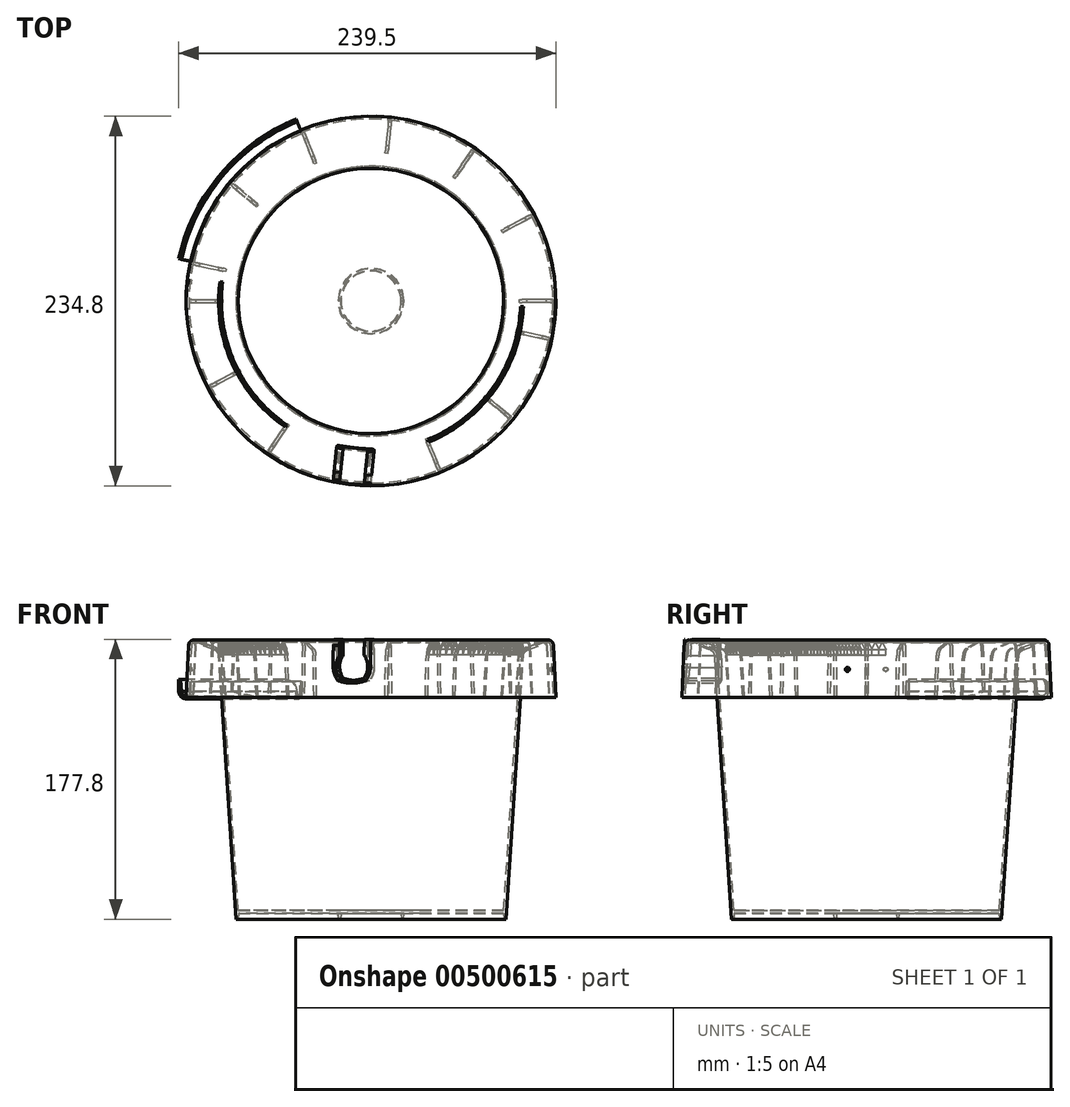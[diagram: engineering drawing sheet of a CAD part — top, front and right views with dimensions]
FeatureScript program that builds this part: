
annotation { "Feature Type Name" : "Feature", "Feature Type Description" : "" }
export const myFeature = defineFeature(function(context is Context, id is Id, definition is map)
    precondition{}
    {
        {
            var Q0;
            Q0=qCreatedBy(makeId("Front.planeOp"),FACE);
            var sketch = newSketch(context, id + "F0", { "sketchPlane" : qUnion([Q0])});
            skLineSegment(sketch, "E0", {"start": v(20.57, 0) * mm, "end": v(19.3, 0) * mm});
            skLineSegment(sketch, "E1", {"start": v(19.3, 0) * mm, "end": v(19.05, 3.81) * mm});
            skLineSegment(sketch, "E2", {"start": v(20.83, 3.81) * mm, "end": v(20.57, 0) * mm});
            skLineSegment(sketch, "E3", {"start": v(0, 0) * mm, "end": v(0, 3.81) * mm});
            skLineSegment(sketch, "E4", {"start": v(0, 3.81) * mm, "end": v(19.05, 3.81) * mm});
            skLineSegment(sketch, "E5", {"start": v(0, 3.81) * mm, "end": v(0, 5.59) * mm});
            skLineSegment(sketch, "E6", {"start": v(0, 5.59) * mm, "end": v(84.3, 5.59) * mm});
            skLineSegment(sketch, "E7", {"start": v(20.83, 3.81) * mm, "end": v(84.3, 3.8) * mm});
            skLineSegment(sketch, "E8", {"start": v(0, 0) * mm, "end": v(0, 179.07) * mm});
            skLineSegment(sketch, "E9", {"start": v(0, 0) * mm, "end": v(0, 171.45) * mm});
            skLineSegment(sketch, "E10", {"start": v(115.62, 140.97) * mm, "end": v(117.4, 140.97) * mm});
            skArc(sketch, "E11", {"start": v(114.08, 174.01) * mm, "mid": v(113.25, 175.47) * mm, "end": v(111.59, 175.66) * mm});
            skLineSegment(sketch, "E12", {"start": v(114.08, 174.01) * mm, "end": v(115.62, 140.97) * mm});
            skLineSegment(sketch, "E13", {"start": v(111.59, 175.66) * mm, "end": v(110.96, 177.33) * mm});
            skLineSegment(sketch, "E14", {"start": v(114.08, 174.01) * mm, "end": v(115.86, 174.1) * mm});
            skLineSegment(sketch, "E15", {"start": v(115.86, 174.1) * mm, "end": v(117.4, 140.97) * mm});
            skArc(sketch, "E16", {"start": v(99.32, 171.08) * mm, "mid": v(97.55, 169.74) * mm, "end": v(96.78, 167.65) * mm});
            skLineSegment(sketch, "E17", {"start": v(96.78, 167.65) * mm, "end": v(85.73, 0) * mm});
            skLineSegment(sketch, "E18", {"start": v(99.32, 171.08) * mm, "end": v(111.59, 175.66) * mm});
            skLineSegment(sketch, "E19", {"start": v(96.78, 167.65) * mm, "end": v(95, 167.77) * mm});
            skLineSegment(sketch, "E20", {"start": v(99.32, 171.08) * mm, "end": v(98.7, 172.74) * mm});
            skLineSegment(sketch, "E21", {"start": v(110.96, 177.33) * mm, "end": v(98.7, 172.74) * mm});
            skLineSegment(sketch, "E22", {"start": v(95, 167.77) * mm, "end": v(84.3, 5.59) * mm});
            skArc(sketch, "E23", {"start": v(98.7, 172.74) * mm, "mid": v(96.12, 170.8) * mm, "end": v(95, 167.77) * mm});
            skLineSegment(sketch, "E24", {"start": v(84.3, 3.8) * mm, "end": v(84.18, 3.8) * mm, "construction": true});
            skLineSegment(sketch, "E25", {"start": v(85.73, 0) * mm, "end": v(84.38, 0) * mm});
            skLineSegment(sketch, "E26", {"start": v(84.18, 3.8) * mm, "end": v(84.38, 0) * mm});
            skLineSegment(sketch, "E27", {"start": v(117.4, 140.97) * mm, "end": v(0, 140.97) * mm, "construction": true});
            skLineSegment(sketch, "E28", {"start": v(95, 167.77) * mm, "end": v(0, 167.77) * mm, "construction": true});
            skLineSegment(sketch, "E29", {"start": v(0, 177.33) * mm, "end": v(0, 179.1) * mm});
            skLineSegment(sketch, "E30", {"start": v(116.18, 167.13) * mm, "end": v(117.96, 167.13) * mm, "construction": true});
            skLineSegment(sketch, "E31", {"start": v(116.18, 167.13) * mm, "end": v(117.96, 167.13) * mm});
            skPoint(sketch, "E32.orphan", {"position": v(120.3, 167.13) * mm});
            skPoint(sketch, "E33.orphan", {"position": v(115.62, 167.13) * mm});
            skLineSegment(sketch, "E34", {"start": v(117.63, 174.1) * mm, "end": v(117.96, 167.13) * mm, "construction": true});
            skLineSegment(sketch, "E35", {"start": v(117.96, 167.13) * mm, "end": v(117.63, 174.1) * mm});
            skPoint(sketch, "E36.start.orphan", {"position": v(115.7, 177.55) * mm});
            skArc(sketch, "E37", {"start": v(117.63, 174.1) * mm, "mid": v(115.95, 177.7) * mm, "end": v(112.23, 179.07) * mm});
            skArc(sketch, "E38", {"start": v(115.86, 174.1) * mm, "mid": v(114.23, 176.96) * mm, "end": v(110.96, 177.33) * mm});
            skSolve(sketch);
        }
        {
            var Q0;
            Q0=qSketchRegion(id+"F0",true);
            var Q1;
            Q1=sQuery(id+"F0.wireOp",EDGE,"E9");
            revolve(context, id + "F1", {"entities" : qUnion([Q0]), "axis" : qUnion([Q1]), "revolveType" : RevolveType.FULL});
        }
        {
            var Q0;
            Q0=qCreatedBy(makeId("Front.planeOp"),FACE);
            var sketch = newSketch(context, id + "F2", { "sketchPlane" : qUnion([Q0])});
            skLineSegment(sketch, "E39", {"start": v(0, 0) * mm, "end": v(0, 3.8) * mm});
            skLineSegment(sketch, "E40", {"start": v(0, 3.8) * mm, "end": v(0, 5.59) * mm});
            skLineSegment(sketch, "E41", {"start": v(0, 0) * mm, "end": v(0, 179.07) * mm});
            skLineSegment(sketch, "E42", {"start": v(0, 0) * mm, "end": v(0, 171.45) * mm});
            skLineSegment(sketch, "E43", {"start": v(0, 179.07) * mm, "end": v(157.98, 179.07) * mm, "construction": true});
            skLineSegment(sketch, "E44", {"start": v(0, 179.07) * mm, "end": v(115.62, 179.07) * mm, "construction": true});
            skLineSegment(sketch, "E45", {"start": v(114.08, 174.01) * mm, "end": v(115.62, 140.97) * mm});
            skLineSegment(sketch, "E46", {"start": v(0, 177.55) * mm, "end": v(129.4, 177.55) * mm, "construction": true});
            skLineSegment(sketch, "E47", {"start": v(111.31, 176.37) * mm, "end": v(99.06, 171.79) * mm});
            skLineSegment(sketch, "E48", {"start": v(94.26, 140.97) * mm, "end": v(96.02, 167.65) * mm});
            skArc(sketch, "E49", {"start": v(99.06, 171.79) * mm, "mid": v(96.93, 170.16) * mm, "end": v(96.02, 167.65) * mm});
            skArc(sketch, "E50", {"start": v(114.08, 174.01) * mm, "mid": v(113.2, 175.8) * mm, "end": v(111.31, 176.37) * mm});
            skLineSegment(sketch, "E51", {"start": v(115.62, 140.97) * mm, "end": v(94.26, 140.97) * mm});
            skSolve(sketch);
        }
        {
            var Q0;
            Q0=makeQuery(id+"F2.imprint","IMPRINT",FACE,{"disambiguationData":[TD([[makeQuery(id+"F2.imprint","IMPRINT",EDGE,{"derivedFrom":sQuery(id+"F2.wireOp",EDGE,"E45")}),-1.0]])]});
            extrude(context, id + "F3", {"entities" : qUnion([Q0]), "endBound" : BoundingType.SYMMETRIC, "depth" : 1.78 * mm});
        }
        {
            var Q0;
            Q0=makeQuery(id+"F3.opExtrude","SWEPT_BODY",BODY,{"disambiguationData":[OSD([sQuery(id+"F2.wireOp",EDGE,"E45"),sQuery(id+"F2.wireOp",EDGE,"E47"),sQuery(id+"F2.wireOp",EDGE,"E48"),sQuery(id+"F2.wireOp",EDGE,"E49"),sQuery(id+"F2.wireOp",EDGE,"E50"),sQuery(id+"F2.wireOp",EDGE,"E51")])]});
            var Q1;
            Q1=makeQuery(id+"F1.opRevolve","SWEPT_FACE",FACE,{"disambiguationData":[OSD([sQuery(id+"F0.wireOp",EDGE,"E15")])]});
            circularPattern(context, id + "F4", {"entities" : qUnion([Q0]), "axis" : qUnion([Q1]), "angle" : 12 * degree, "instanceCount" : 2, "equalSpace" : true});
        }
        {
            var Q0;
            Q0=makeQuery(id+"F3.opExtrude","SWEPT_BODY",BODY,{"disambiguationData":[OSD([sQuery(id+"F2.wireOp",EDGE,"E45"),sQuery(id+"F2.wireOp",EDGE,"E47"),sQuery(id+"F2.wireOp",EDGE,"E48"),sQuery(id+"F2.wireOp",EDGE,"E49"),sQuery(id+"F2.wireOp",EDGE,"E50"),sQuery(id+"F2.wireOp",EDGE,"E51")])]});
            var Q1;
            Q1=makeQuery(id+"F1.opRevolve","SWEPT_FACE",FACE,{"disambiguationData":[OSD([sQuery(id+"F0.wireOp",EDGE,"E12")])]});
            circularPattern(context, id + "F5", {"entities" : qUnion([Q0]), "axis" : qUnion([Q1]), "angle" : 28 * degree, "instanceCount" : 2, "equalSpace" : true});
        }
        {
            var Q0;
            Q0=makeQuery(id+"F3.opExtrude","SWEPT_BODY",BODY,{"disambiguationData":[OSD([sQuery(id+"F2.wireOp",EDGE,"E45"),sQuery(id+"F2.wireOp",EDGE,"E47"),sQuery(id+"F2.wireOp",EDGE,"E48"),sQuery(id+"F2.wireOp",EDGE,"E49"),sQuery(id+"F2.wireOp",EDGE,"E50"),sQuery(id+"F2.wireOp",EDGE,"E51")])]});
            var Q1;
            Q1=makeQuery(id+"F1.opRevolve","SWEPT_FACE",FACE,{"disambiguationData":[OSD([sQuery(id+"F0.wireOp",EDGE,"E12")])]});
            circularPattern(context, id + "F6", {"entities" : qUnion([Q0]), "axis" : qUnion([Q1]), "angle" : 56 * degree, "instanceCount" : 2, "equalSpace" : true});
        }
        {
            var Q0;
            Q0=makeQuery(id+"F3.opExtrude","SWEPT_BODY",BODY,{"disambiguationData":[OSD([sQuery(id+"F2.wireOp",EDGE,"E45"),sQuery(id+"F2.wireOp",EDGE,"E47"),sQuery(id+"F2.wireOp",EDGE,"E48"),sQuery(id+"F2.wireOp",EDGE,"E49"),sQuery(id+"F2.wireOp",EDGE,"E50"),sQuery(id+"F2.wireOp",EDGE,"E51")])]});
            var Q1;
            Q1=makeQuery(id+"F1.opRevolve","SWEPT_FACE",FACE,{"disambiguationData":[OSD([sQuery(id+"F0.wireOp",EDGE,"E12")])]});
            circularPattern(context, id + "F7", {"entities" : qUnion([Q0]), "axis" : qUnion([Q1]), "angle" : 84 * degree, "instanceCount" : 2, "equalSpace" : true});
        }
        {
            var Q0;
            Q0=makeQuery(id+"F1.opRevolve","SWEPT_BODY",BODY,{"disambiguationData":[OSD([sQuery(id+"F0.wireOp",EDGE,"E0"),sQuery(id+"F0.wireOp",EDGE,"E1"),sQuery(id+"F0.wireOp",EDGE,"E2"),sQuery(id+"F0.wireOp",EDGE,"E4"),sQuery(id+"F0.wireOp",EDGE,"E6"),sQuery(id+"F0.wireOp",EDGE,"E7"),sQuery(id+"F0.wireOp",EDGE,"E9"),sQuery(id+"F0.wireOp",EDGE,"E10"),sQuery(id+"F0.wireOp",EDGE,"E11"),sQuery(id+"F0.wireOp",EDGE,"E12"),sQuery(id+"F0.wireOp",EDGE,"E15"),sQuery(id+"F0.wireOp",EDGE,"LKbFe0pn-6IGS-4NvF-Y8YP-ZpA0iSk9hzCY"),sQuery(id+"F0.wireOp",EDGE,"E16"),sQuery(id+"F0.wireOp",EDGE,"E17"),sQuery(id+"F0.wireOp",EDGE,"E18"),sQuery(id+"F0.wireOp",EDGE,"E21"),sQuery(id+"F0.wireOp",EDGE,"E22"),sQuery(id+"F0.wireOp",EDGE,"E23"),sQuery(id+"F0.wireOp",EDGE,"E25"),sQuery(id+"F0.wireOp",EDGE,"E26")])]});
            var Q1;
            Q1=makeQuery(id+"F3.opExtrude","SWEPT_BODY",BODY,{"disambiguationData":[OSD([sQuery(id+"F2.wireOp",EDGE,"E45"),sQuery(id+"F2.wireOp",EDGE,"E47"),sQuery(id+"F2.wireOp",EDGE,"E48"),sQuery(id+"F2.wireOp",EDGE,"E49"),sQuery(id+"F2.wireOp",EDGE,"E50"),sQuery(id+"F2.wireOp",EDGE,"E51")])]});
            var Q2;
            Q2=makeQuery(id+"F1.opRevolve","SWEPT_FACE",FACE,{"disambiguationData":[OSD([sQuery(id+"F0.wireOp",EDGE,"E12")])]});
            circularPattern(context, id + "F8", {"entities" : qUnion([Q0, Q1]), "axis" : qUnion([Q2]), "angle" : 112 * degree, "instanceCount" : 2, "equalSpace" : true});
        }
        {
            var Q0;
            Q0=makeQuery(id+"F3.opExtrude","SWEPT_BODY",BODY,{"disambiguationData":[OSD([sQuery(id+"F2.wireOp",EDGE,"E45"),sQuery(id+"F2.wireOp",EDGE,"E47"),sQuery(id+"F2.wireOp",EDGE,"E48"),sQuery(id+"F2.wireOp",EDGE,"E49"),sQuery(id+"F2.wireOp",EDGE,"E50"),sQuery(id+"F2.wireOp",EDGE,"E51")])]});
            var Q1;
            Q1=makeQuery(id+"F8.opPattern","COPY",FACE,{"derivedFrom":makeQuery(id+"F1.opRevolve","SWEPT_FACE",FACE,{"disambiguationData":[OSD([sQuery(id+"F0.wireOp",EDGE,"E12")])]}),"instanceName":"1"});
            circularPattern(context, id + "F9", {"entities" : qUnion([Q0]), "axis" : qUnion([Q1]), "angle" : 140 * degree, "instanceCount" : 2, "equalSpace" : true});
        }
        {
            var Q0;
            Q0=makeQuery(id+"F3.opExtrude","SWEPT_BODY",BODY,{"disambiguationData":[OSD([sQuery(id+"F2.wireOp",EDGE,"E45"),sQuery(id+"F2.wireOp",EDGE,"E47"),sQuery(id+"F2.wireOp",EDGE,"E48"),sQuery(id+"F2.wireOp",EDGE,"E49"),sQuery(id+"F2.wireOp",EDGE,"E50"),sQuery(id+"F2.wireOp",EDGE,"E51")])]});
            var Q1;
            Q1=makeQuery(id+"F8.opPattern","COPY",FACE,{"derivedFrom":makeQuery(id+"F1.opRevolve","SWEPT_FACE",FACE,{"disambiguationData":[OSD([sQuery(id+"F0.wireOp",EDGE,"E12")])]}),"instanceName":"1"});
            circularPattern(context, id + "F10", {"entities" : qUnion([Q0]), "axis" : qUnion([Q1]), "angle" : 168 * degree, "instanceCount" : 2, "equalSpace" : true});
        }
        {
            var Q0;
            Q0=makeQuery(id+"F3.opExtrude","SWEPT_BODY",BODY,{"disambiguationData":[OSD([sQuery(id+"F2.wireOp",EDGE,"E45"),sQuery(id+"F2.wireOp",EDGE,"E47"),sQuery(id+"F2.wireOp",EDGE,"E48"),sQuery(id+"F2.wireOp",EDGE,"E49"),sQuery(id+"F2.wireOp",EDGE,"E50"),sQuery(id+"F2.wireOp",EDGE,"E51")])]});
            var Q1;
            Q1=makeQuery(id+"F1.opRevolve","SWEPT_FACE",FACE,{"disambiguationData":[OSD([sQuery(id+"F0.wireOp",EDGE,"E11")])]});
            circularPattern(context, id + "F11", {"entities" : qUnion([Q0]), "axis" : qUnion([Q1]), "angle" : 180 * degree, "instanceCount" : 2, "equalSpace" : true});
        }
        {
            var Q0;
            Q0=makeQuery(id+"F3.opExtrude","SWEPT_BODY",BODY,{"disambiguationData":[OSD([sQuery(id+"F2.wireOp",EDGE,"E45"),sQuery(id+"F2.wireOp",EDGE,"E47"),sQuery(id+"F2.wireOp",EDGE,"E48"),sQuery(id+"F2.wireOp",EDGE,"E49"),sQuery(id+"F2.wireOp",EDGE,"E50"),sQuery(id+"F2.wireOp",EDGE,"E51")])]});
            var Q1;
            Q1=makeQuery(id+"F8.opPattern","COPY",FACE,{"derivedFrom":makeQuery(id+"F1.opRevolve","SWEPT_FACE",FACE,{"disambiguationData":[OSD([sQuery(id+"F0.wireOp",EDGE,"E15")])]}),"instanceName":"1"});
            circularPattern(context, id + "F12", {"entities" : qUnion([Q0]), "axis" : qUnion([Q1]), "angle" : 208 * degree, "instanceCount" : 2, "oppositeDirection" : true, "equalSpace" : true});
        }
        {
            var Q0;
            Q0=makeQuery(id+"F3.opExtrude","SWEPT_BODY",BODY,{"disambiguationData":[OSD([sQuery(id+"F2.wireOp",EDGE,"E45"),sQuery(id+"F2.wireOp",EDGE,"E47"),sQuery(id+"F2.wireOp",EDGE,"E48"),sQuery(id+"F2.wireOp",EDGE,"E49"),sQuery(id+"F2.wireOp",EDGE,"E50"),sQuery(id+"F2.wireOp",EDGE,"E51")])]});
            var Q1;
            Q1=makeQuery(id+"F1.opRevolve","SWEPT_FACE",FACE,{"disambiguationData":[OSD([sQuery(id+"F0.wireOp",EDGE,"E15")])]});
            circularPattern(context, id + "F13", {"entities" : qUnion([Q0]), "axis" : qUnion([Q1]), "angle" : 236 * degree, "instanceCount" : 2, "oppositeDirection" : true, "equalSpace" : true});
        }
        {
            var Q0;
            Q0=makeQuery(id+"F3.opExtrude","SWEPT_BODY",BODY,{"disambiguationData":[OSD([sQuery(id+"F2.wireOp",EDGE,"E45"),sQuery(id+"F2.wireOp",EDGE,"E47"),sQuery(id+"F2.wireOp",EDGE,"E48"),sQuery(id+"F2.wireOp",EDGE,"E49"),sQuery(id+"F2.wireOp",EDGE,"E50"),sQuery(id+"F2.wireOp",EDGE,"E51")])]});
            var Q1;
            Q1=makeQuery(id+"F8.opPattern","COPY",FACE,{"derivedFrom":makeQuery(id+"F1.opRevolve","SWEPT_FACE",FACE,{"disambiguationData":[OSD([sQuery(id+"F0.wireOp",EDGE,"E12")])]}),"instanceName":"1"});
            circularPattern(context, id + "F14", {"entities" : qUnion([Q0]), "axis" : qUnion([Q1]), "angle" : 40 * degree, "instanceCount" : 2, "oppositeDirection" : true, "equalSpace" : true});
        }
        {
            var Q0;
            Q0=makeQuery(id+"F3.opExtrude","SWEPT_BODY",BODY,{"disambiguationData":[OSD([sQuery(id+"F2.wireOp",EDGE,"E45"),sQuery(id+"F2.wireOp",EDGE,"E47"),sQuery(id+"F2.wireOp",EDGE,"E48"),sQuery(id+"F2.wireOp",EDGE,"E49"),sQuery(id+"F2.wireOp",EDGE,"E50"),sQuery(id+"F2.wireOp",EDGE,"E51")])]});
            var Q1;
            Q1=makeQuery(id+"F1.opRevolve","SWEPT_FACE",FACE,{"disambiguationData":[OSD([sQuery(id+"F0.wireOp",EDGE,"E12")])]});
            circularPattern(context, id + "F15", {"entities" : qUnion([Q0]), "axis" : qUnion([Q1]), "angle" : 68 * degree, "instanceCount" : 2, "oppositeDirection" : true, "equalSpace" : true});
        }
        {
            var Q0;
            Q0=makeQuery(id+"F4.opPattern","COPY",FACE,{"derivedFrom":makeQuery(id+"F3.opExtrude","CAP_FACE",FACE,{"disambiguationData":[OSD([sQuery(id+"F2.wireOp",EDGE,"E45"),sQuery(id+"F2.wireOp",EDGE,"E47"),sQuery(id+"F2.wireOp",EDGE,"E48"),sQuery(id+"F2.wireOp",EDGE,"E49"),sQuery(id+"F2.wireOp",EDGE,"E50"),sQuery(id+"F2.wireOp",EDGE,"E51")])],"isStart":false}),"instanceName":"1"});
            var Q1;
            Q1=makeQuery(id+"F3.opExtrude","CAP_FACE",FACE,{"disambiguationData":[OSD([sQuery(id+"F2.wireOp",EDGE,"E45"),sQuery(id+"F2.wireOp",EDGE,"E47"),sQuery(id+"F2.wireOp",EDGE,"E48"),sQuery(id+"F2.wireOp",EDGE,"E49"),sQuery(id+"F2.wireOp",EDGE,"E50"),sQuery(id+"F2.wireOp",EDGE,"E51")])],"isStart":true});
            cPlane(context, id + "F16", {"entities" : qUnion([Q0, Q1]), "cplaneType" : CPlaneType.MID_PLANE, "offset" : 25.4 * mm, "width" : 152.4 * mm, "height" : 152.4 * mm});
        }
        {
            var Q0;
            Q0=qCreatedBy(id+"F16.planeOp",FACE);
            cPlane(context, id + "F17", {"entities" : qUnion([Q0]), "cplaneType" : CPlaneType.OFFSET, "offset" : 127 * mm, "width" : 152.4 * mm, "height" : 152.4 * mm});
        }
        {
            var Q0;
            Q0=makeQuery(id+"F7.opPattern","COPY",FACE,{"derivedFrom":makeQuery(id+"F3.opExtrude","CAP_FACE",FACE,{"disambiguationData":[OSD([sQuery(id+"F2.wireOp",EDGE,"E45"),sQuery(id+"F2.wireOp",EDGE,"E47"),sQuery(id+"F2.wireOp",EDGE,"E48"),sQuery(id+"F2.wireOp",EDGE,"E49"),sQuery(id+"F2.wireOp",EDGE,"E50"),sQuery(id+"F2.wireOp",EDGE,"E51")])],"isStart":false}),"instanceName":"1"});
            cPlane(context, id + "F18", {"entities" : qUnion([Q0]), "cplaneType" : CPlaneType.OFFSET, "offset" : 0.89 * mm, "oppositeDirection" : true, "width" : 152.4 * mm, "height" : 152.4 * mm});
        }
        {
            var Q0;
            Q0=qCreatedBy(id+"F18.planeOp",FACE);
            cPlane(context, id + "F19", {"entities" : qUnion([Q0]), "cplaneType" : CPlaneType.OFFSET, "offset" : 127 * mm, "width" : 152.4 * mm, "height" : 152.4 * mm});
        }
        {
            var Q0;
            Q0=qCreatedBy(id+"F19.planeOp",FACE);
            var sketch = newSketch(context, id + "F20", { "sketchPlane" : qUnion([Q0])});
            skLineSegment(sketch, "E52", {"start": v(0, 0) * mm, "end": v(0, 158.75) * mm, "construction": true});
            skCircle(sketch, "E53", {"center": v(0, 158.75) * mm, "radius": 1.27 * mm});
            skSolve(sketch);
        }
        {
            var Q0;
            Q0=makeQuery(id+"F20.imprint","IMPRINT",FACE,{"disambiguationData":[TD([[makeQuery(id+"F20.imprint","IMPRINT",EDGE,{"derivedFrom":sQuery(id+"F20.wireOp",EDGE,"E53")}),1.0]])]});
            extrude(context, id + "F21", {"entities" : qUnion([Q0]), "operationType" : NewBodyOperationType.REMOVE, "oppositeDirection" : true, "depth" : 25.4 * mm});
        }
        {
            var Q0;
            Q0=qCreatedBy(id+"F19.planeOp",FACE);
            cPlane(context, id + "F22", {"entities" : qUnion([Q0]), "cplaneType" : CPlaneType.OFFSET, "offset" : 254 * mm, "oppositeDirection" : true, "width" : 152.4 * mm, "height" : 152.4 * mm});
        }
        {
            var Q0;
            Q0=qCreatedBy(id+"F22.planeOp",FACE);
            var sketch = newSketch(context, id + "F23", { "sketchPlane" : qUnion([Q0])});
            skLineSegment(sketch, "E54", {"start": v(0, 0) * mm, "end": v(0, 158.75) * mm, "construction": true});
            skCircle(sketch, "E55", {"center": v(0, 158.75) * mm, "radius": 1.27 * mm});
            skSolve(sketch);
        }
        {
            var Q0;
            Q0=makeQuery(id+"F23.imprint","IMPRINT",FACE,{"disambiguationData":[TD([[makeQuery(id+"F23.imprint","IMPRINT",EDGE,{"derivedFrom":sQuery(id+"F23.wireOp",EDGE,"E55")}),1.0]])]});
            extrude(context, id + "F24", {"entities" : qUnion([Q0]), "operationType" : NewBodyOperationType.REMOVE, "depth" : 25.4 * mm});
        }
        {
            var Q0;
            Q0=qCreatedBy(id+"F17.planeOp",FACE);
            cPlane(context, id + "F25", {"entities" : qUnion([Q0]), "cplaneType" : CPlaneType.OFFSET, "offset" : 25.4 * mm, "oppositeDirection" : true, "width" : 152.4 * mm, "height" : 152.4 * mm});
        }
        {
            var Q0;
            Q0=qCreatedBy(id+"F16.planeOp",FACE);
            var sketch = newSketch(context, id + "F26", { "sketchPlane" : qUnion([Q0])});
            skLineSegment(sketch, "E56", {"start": v(0, 0) * mm, "end": v(-95, 0) * mm, "construction": true});
            skLineSegment(sketch, "E57", {"start": v(-95, 0) * mm, "end": v(-95, 167.77) * mm, "construction": true});
            skLineSegment(sketch, "E58", {"start": v(-95, 167.77) * mm, "end": v(-95, 176.02) * mm});
            skLineSegment(sketch, "E59", {"start": v(-95, 176.02) * mm, "end": v(-96.77, 176.02) * mm});
            skLineSegment(sketch, "E60", {"start": v(-96.77, 176.02) * mm, "end": v(-96.77, 171.3) * mm});
            skLineSegment(sketch, "E61", {"start": v(-95, 167.77) * mm, "end": v(-96.77, 171.3) * mm});
            skSolve(sketch);
        }
        {
            var Q0;
            Q0=makeQuery(id+"F26.imprint","IMPRINT",FACE,{"disambiguationData":[TD([[makeQuery(id+"F26.imprint","IMPRINT",EDGE,{"derivedFrom":sQuery(id+"F26.wireOp",EDGE,"E58")}),1.0]])]});
            extrude(context, id + "F27", {"entities" : qUnion([Q0]), "depth" : 2.22 * mm, "hasSecondDirection" : true, "secondDirectionOppositeDirection" : true, "secondDirectionDepth" : 2.22 * mm});
        }
        {
            var Q0;
            Q0=makeQuery(id+"F27.opExtrude","SWEPT_FACE",FACE,{"disambiguationData":[OSD([sQuery(id+"F26.wireOp",EDGE,"E60")])]});
            var sketch = newSketch(context, id + "F28", { "sketchPlane" : qUnion([Q0])});
            skLineSegment(sketch, "E62", {"start": v(2.22, 176.02) * mm, "end": v(2.22, 171.63) * mm});
            skLineSegment(sketch, "E63", {"start": v(2.22, 171.63) * mm, "end": v(0, 176.02) * mm});
            skLineSegment(sketch, "E64", {"start": v(0, 176.02) * mm, "end": v(2.22, 176.02) * mm});
            skSolve(sketch);
        }
        {
            var Q0;
            Q0=makeQuery(id+"F28.imprint","IMPRINT",FACE,{"disambiguationData":[TD([[makeQuery(id+"F28.imprint","IMPRINT",EDGE,{"derivedFrom":sQuery(id+"F28.wireOp",EDGE,"E62")}),-1.0]])]});
            extrude(context, id + "F29", {"entities" : qUnion([Q0]), "operationType" : NewBodyOperationType.REMOVE, "oppositeDirection" : true, "depth" : 25.4 * mm});
        }
        {
            var Q0;
            Q0=makeQuery(id+"F27.opExtrude","SWEPT_FACE",FACE,{"disambiguationData":[OSD([sQuery(id+"F26.wireOp",EDGE,"E60")])]});
            var sketch = newSketch(context, id + "F30", { "sketchPlane" : qUnion([Q0])});
            skLineSegment(sketch, "E65", {"start": v(0, 176.02) * mm, "end": v(-2.22, 176.02) * mm});
            skLineSegment(sketch, "E66", {"start": v(-2.22, 176.02) * mm, "end": v(-2.22, 171.64) * mm});
            skLineSegment(sketch, "E67", {"start": v(-2.22, 171.64) * mm, "end": v(0, 176.02) * mm});
            skSolve(sketch);
        }
        {
            var Q0;
            Q0=makeQuery(id+"F30.imprint","IMPRINT",FACE,{"disambiguationData":[TD([[makeQuery(id+"F30.imprint","IMPRINT",EDGE,{"derivedFrom":sQuery(id+"F30.wireOp",EDGE,"E65")}),1.0]])]});
            extrude(context, id + "F31", {"entities" : qUnion([Q0]), "operationType" : NewBodyOperationType.REMOVE, "oppositeDirection" : true, "depth" : 25.4 * mm});
        }
        {
            var Q0;
            Q0=makeQuery(id+"F27.opExtrude","SWEPT_BODY",BODY,{"disambiguationData":[OSD([sQuery(id+"F26.wireOp",EDGE,"E58"),sQuery(id+"F26.wireOp",EDGE,"E59"),sQuery(id+"F26.wireOp",EDGE,"E60"),sQuery(id+"F26.wireOp",EDGE,"E61")])]});
            var Q1;
            Q1=makeQuery(id+"F1.opRevolve","SWEPT_FACE",FACE,{"disambiguationData":[OSD([sQuery(id+"F0.wireOp",EDGE,"E22")])]});
            circularPattern(context, id + "F32", {"entities" : qUnion([Q0]), "axis" : qUnion([Q1]), "angle" : 60.5 * degree, "instanceCount" : 24, "oppositeDirection" : true, "equalSpace" : true});
        }
        {
            var Q0;
            Q0=makeQuery(id+"F32.opPattern","COPY",BODY,{"derivedFrom":makeQuery(id+"F27.opExtrude","SWEPT_BODY",BODY,{"disambiguationData":[OSD([sQuery(id+"F26.wireOp",EDGE,"E58"),sQuery(id+"F26.wireOp",EDGE,"E59"),sQuery(id+"F26.wireOp",EDGE,"E60"),sQuery(id+"F26.wireOp",EDGE,"E61")])]}),"instanceName":"1"});
            var Q1;
            Q1=makeQuery(id+"F27.opExtrude","SWEPT_BODY",BODY,{"disambiguationData":[OSD([sQuery(id+"F26.wireOp",EDGE,"E58"),sQuery(id+"F26.wireOp",EDGE,"E59"),sQuery(id+"F26.wireOp",EDGE,"E60"),sQuery(id+"F26.wireOp",EDGE,"E61")])]});
            var Q2;
            Q2=makeQuery(id+"F8.opPattern","COPY",FACE,{"derivedFrom":makeQuery(id+"F1.opRevolve","SWEPT_FACE",FACE,{"disambiguationData":[OSD([sQuery(id+"F0.wireOp",EDGE,"E15")])]}),"instanceName":"1"});
            circularPattern(context, id + "F33", {"entities" : qUnion([Q0, Q1]), "axis" : qUnion([Q2]), "angle" : 180 * degree, "instanceCount" : 2, "oppositeDirection" : true, "equalSpace" : true});
        }
        {
            var Q0;
            Q0=makeQuery(id+"F33.opPattern","COPY",BODY,{"derivedFrom":makeQuery(id+"F32.opPattern","COPY",BODY,{"derivedFrom":makeQuery(id+"F27.opExtrude","SWEPT_BODY",BODY,{"disambiguationData":[OSD([sQuery(id+"F26.wireOp",EDGE,"E58"),sQuery(id+"F26.wireOp",EDGE,"E59"),sQuery(id+"F26.wireOp",EDGE,"E60"),sQuery(id+"F26.wireOp",EDGE,"E61")])]}),"instanceName":"1"}),"instanceName":"1"});
            var Q1;
            Q1=makeQuery(id+"F33.opPattern","COPY",BODY,{"derivedFrom":makeQuery(id+"F27.opExtrude","SWEPT_BODY",BODY,{"disambiguationData":[OSD([sQuery(id+"F26.wireOp",EDGE,"E58"),sQuery(id+"F26.wireOp",EDGE,"E59"),sQuery(id+"F26.wireOp",EDGE,"E60"),sQuery(id+"F26.wireOp",EDGE,"E61")])]}),"instanceName":"1"});
            var Q2;
            Q2=makeQuery(id+"F1.opRevolve","SWEPT_FACE",FACE,{"disambiguationData":[OSD([sQuery(id+"F0.wireOp",EDGE,"E21")])]});
            circularPattern(context, id + "F34", {"entities" : qUnion([Q0, Q1]), "axis" : qUnion([Q2]), "angle" : 60.5 * degree, "instanceCount" : 24, "equalSpace" : true});
        }
        {
            var Q0;
            Q0=makeQuery(id+"F10.opPattern","COPY",FACE,{"derivedFrom":makeQuery(id+"F3.opExtrude","CAP_FACE",FACE,{"disambiguationData":[OSD([sQuery(id+"F2.wireOp",EDGE,"E45"),sQuery(id+"F2.wireOp",EDGE,"E47"),sQuery(id+"F2.wireOp",EDGE,"E48"),sQuery(id+"F2.wireOp",EDGE,"E49"),sQuery(id+"F2.wireOp",EDGE,"E50"),sQuery(id+"F2.wireOp",EDGE,"E51")])],"isStart":false}),"instanceName":"1"});
            var sketch = newSketch(context, id + "F35", { "sketchPlane" : qUnion([Q0])});
            skLineSegment(sketch, "E68", {"start": v(115.5, 140.97) * mm, "end": v(115.05, 151.12) * mm});
            skLineSegment(sketch, "E69", {"start": v(117.3, 151.12) * mm, "end": v(118.28, 141.1) * mm});
            skLineSegment(sketch, "E70", {"start": v(117.3, 151.12) * mm, "end": v(115.05, 151.12) * mm});
            skLineSegment(sketch, "E71", {"start": v(118.28, 141.1) * mm, "end": v(118.46, 139.23) * mm});
            skLineSegment(sketch, "E72", {"start": v(115.5, 140.97) * mm, "end": v(115.5, 139.25) * mm});
            skLineSegment(sketch, "E73", {"start": v(115.5, 139.25) * mm, "end": v(118.46, 139.23) * mm});
            skSolve(sketch);
        }
        {
            var Q0;
            {var subQ2=sQuery(id+"F35.wireOp",EDGE,"E69");Q0=makeQuery(id+"F35.imprint","IMPRINT",FACE,{"disambiguationData":[TD([[makeQuery(id+"F35.imprint","IMPRINT",EDGE,{"derivedFrom":subQ2}),-1.0]])]});}
            var Q1;
            Q1=makeQuery(id+"F8.opPattern","COPY",FACE,{"derivedFrom":makeQuery(id+"F1.opRevolve","SWEPT_FACE",FACE,{"disambiguationData":[OSD([sQuery(id+"F0.wireOp",EDGE,"E15")])]}),"instanceName":"1"});
            revolve(context, id + "F36", {"operationType" : NewBodyOperationType.REMOVE, "entities" : qUnion([Q0]), "axis" : qUnion([Q1]), "revolveType" : RevolveType.ONE_DIRECTION, "angle" : 55 * degree});
        }
        {
            var Q0;
            {var subQ0=sQuery(id+"F35.wireOp",EDGE,"E70");Q0=makeQuery(id+"F36.boolean.opBoolean","COPY",FACE,{"disambiguationData":[TD([makeQuery(id+"F8.opPattern","COPY",FACE,{"derivedFrom":makeQuery(id+"F1.opRevolve","SWEPT_FACE",FACE,{"disambiguationData":[OSD([sQuery(id+"F0.wireOp",EDGE,"E10")])]}),"instanceName":"1"})])],"derivedFrom":makeQuery(id+"F36.opRevolve","CAP_FACE",FACE,{"disambiguationData":[OSD([sQuery(id+"F2.wireOp",EDGE,"E45"),sQuery(id+"F2.wireOp",EDGE,"E51"),sQuery(id+"F35.wireOp",EDGE,"E69"),subQ0,sQuery(id+"F35.wireOp",EDGE,"E71"),sQuery(id+"F35.wireOp",EDGE,"E72"),sQuery(id+"F35.wireOp",EDGE,"E73")])],"isStart":true})});}
            var sketch = newSketch(context, id + "F37", { "sketchPlane" : qUnion([Q0])});
            skLineSegment(sketch, "E74", {"start": v(115.62, 140.97) * mm, "end": v(125.02, 140.97) * mm, "construction": true});
            skLineSegment(sketch, "E75", {"start": v(115.62, 140.97) * mm, "end": v(120.32, 140.97) * mm, "construction": true});
            skLineSegment(sketch, "E76", {"start": v(116.92, 151.12) * mm, "end": v(115.15, 151.12) * mm});
            skLineSegment(sketch, "E77", {"start": v(115.15, 151.12) * mm, "end": v(115.44, 144.83) * mm});
            skLineSegment(sketch, "E78", {"start": v(115.44, 144.83) * mm, "end": v(115.44, 144.83) * mm});
            skArc(sketch, "E79", {"start": v(115.44, 144.83) * mm, "mid": v(120.23, 140.04) * mm, "end": v(125.02, 144.83) * mm});
            skLineSegment(sketch, "E80", {"start": v(125.02, 152.45) * mm, "end": v(123.75, 152.45) * mm});
            skLineSegment(sketch, "E81", {"start": v(123.75, 152.45) * mm, "end": v(123.24, 144.83) * mm});
            skLineSegment(sketch, "E82", {"start": v(120.23, 140.97) * mm, "end": v(120.23, 141.82) * mm});
            skArc(sketch, "E83", {"start": v(117.22, 144.83) * mm, "mid": v(120.23, 141.82) * mm, "end": v(123.24, 144.83) * mm});
            skLineSegment(sketch, "E84", {"start": v(116.92, 151.12) * mm, "end": v(117.22, 144.83) * mm});
            skPoint(sketch, "E85.orphan", {"position": v(120.23, 140.04) * mm});
            skLineSegment(sketch, "E86", {"start": v(125.02, 152.45) * mm, "end": v(125.02, 144.83) * mm});
            skSolve(sketch);
        }
        {
            var Q0;
            Q0=makeQuery(id+"F37.imprint","IMPRINT",FACE,{"disambiguationData":[TD([[makeQuery(id+"F37.imprint","IMPRINT",EDGE,{"derivedFrom":sQuery(id+"F37.wireOp",EDGE,"E80")}),1.0]])]});
            var Q1;
            Q1=makeQuery(id+"F37.imprint","IMPRINT",FACE,{"disambiguationData":[TD([[makeQuery(id+"F37.imprint","IMPRINT",EDGE,{"derivedFrom":sQuery(id+"F37.wireOp",EDGE,"E76")}),1.0]])]});
            var Q2;
            Q2=makeQuery(id+"F1.opRevolve","SWEPT_FACE",FACE,{"disambiguationData":[OSD([sQuery(id+"F0.wireOp",EDGE,"E15")])]});
            revolve(context, id + "F38", {"entities" : qUnion([Q0, Q1]), "axis" : qUnion([Q2]), "revolveType" : RevolveType.ONE_DIRECTION, "angle" : 55.2 * degree});
        }
        {
            var Q0;
            Q0=makeQuery(id+"F38.opRevolve","CAP_EDGE",EDGE,{"disambiguationData":[OSD([sQuery(id+"F37.wireOp",EDGE,"E80")]),OD(0.0)],"isStart":false});
            var Q1;
            Q1=makeQuery(id+"F38.opRevolve","CAP_EDGE",EDGE,{"disambiguationData":[OSD([sQuery(id+"F37.wireOp",EDGE,"E80")]),OD(1.0)],"isStart":false});
            fillet(context, id + "F39", {"entities" : qUnion([Q0, Q1]), "radius" : 7.62 * mm, "tangentPropagation" : true, "allowEdgeOverflow" : false});
        }
        {
            var Q0;
            Q0=makeQuery(id+"F9.opPattern","COPY",FACE,{"derivedFrom":makeQuery(id+"F3.opExtrude","CAP_FACE",FACE,{"disambiguationData":[OSD([sQuery(id+"F2.wireOp",EDGE,"E45"),sQuery(id+"F2.wireOp",EDGE,"E47"),sQuery(id+"F2.wireOp",EDGE,"E48"),sQuery(id+"F2.wireOp",EDGE,"E49"),sQuery(id+"F2.wireOp",EDGE,"E50"),sQuery(id+"F2.wireOp",EDGE,"E51")])],"isStart":true}),"instanceName":"1"});
            var sketch = newSketch(context, id + "F40", { "sketchPlane" : qUnion([Q0])});
            skLineSegment(sketch, "E87", {"start": v(-115.36, 144.6) * mm, "end": v(-115.62, 140.97) * mm});
            skLineSegment(sketch, "E88", {"start": v(-115.62, 140.97) * mm, "end": v(-94.98, 140.97) * mm});
            skLineSegment(sketch, "E89", {"start": v(-94.98, 140.97) * mm, "end": v(-115.36, 144.6) * mm});
            skSolve(sketch);
        }
        {
            var Q0;
            Q0=makeQuery(id+"F40.imprint","IMPRINT",FACE,{"disambiguationData":[TD([[makeQuery(id+"F40.imprint","IMPRINT",EDGE,{"derivedFrom":sQuery(id+"F40.wireOp",EDGE,"E87")}),1.0]])]});
            extrude(context, id + "F41", {"entities" : qUnion([Q0]), "operationType" : NewBodyOperationType.REMOVE, "oppositeDirection" : true, "depth" : 1.78 * mm});
        }
        {
            var Q0;
            Q0=makeQuery(id+"F9.opPattern","COPY",FACE,{"derivedFrom":makeQuery(id+"F3.opExtrude","CAP_FACE",FACE,{"disambiguationData":[OSD([sQuery(id+"F2.wireOp",EDGE,"E45"),sQuery(id+"F2.wireOp",EDGE,"E47"),sQuery(id+"F2.wireOp",EDGE,"E48"),sQuery(id+"F2.wireOp",EDGE,"E49"),sQuery(id+"F2.wireOp",EDGE,"E50"),sQuery(id+"F2.wireOp",EDGE,"E51")])],"isStart":true}),"instanceName":"1"});
            var sketch = newSketch(context, id + "F42", { "sketchPlane" : qUnion([Q0])});
            skLineSegment(sketch, "E90", {"start": v(-115.62, 140.97) * mm, "end": v(-115.36, 144.6) * mm});
            skLineSegment(sketch, "E91", {"start": v(-115.62, 140.97) * mm, "end": v(-115.45, 144.61) * mm});
            skLineSegment(sketch, "E92", {"start": v(-115.45, 144.61) * mm, "end": v(-115.36, 144.6) * mm});
            skSolve(sketch);
        }
        {
            var Q0;
            Q0=makeQuery(id+"F42.imprint","IMPRINT",FACE,{"disambiguationData":[TD([[makeQuery(id+"F42.imprint","IMPRINT",EDGE,{"derivedFrom":sQuery(id+"F42.wireOp",EDGE,"E90")}),-1.0]])]});
            extrude(context, id + "F43", {"entities" : qUnion([Q0]), "operationType" : NewBodyOperationType.REMOVE, "oppositeDirection" : true, "depth" : 1.78 * mm});
        }
        {
            var Q0;
            {var subQ0=sQuery(id+"F35.wireOp",EDGE,"E70");Q0=makeQuery(id+"F36.boolean.opBoolean","COPY",FACE,{"disambiguationData":[TD([makeQuery(id+"F8.opPattern","COPY",FACE,{"derivedFrom":makeQuery(id+"F1.opRevolve","SWEPT_FACE",FACE,{"disambiguationData":[OSD([sQuery(id+"F0.wireOp",EDGE,"E10")])]}),"instanceName":"1"})])],"derivedFrom":makeQuery(id+"F36.opRevolve","CAP_FACE",FACE,{"disambiguationData":[OSD([sQuery(id+"F2.wireOp",EDGE,"E45"),sQuery(id+"F2.wireOp",EDGE,"E51"),sQuery(id+"F35.wireOp",EDGE,"E69"),subQ0,sQuery(id+"F35.wireOp",EDGE,"E71"),sQuery(id+"F35.wireOp",EDGE,"E72"),sQuery(id+"F35.wireOp",EDGE,"E73")])],"isStart":false})});}
            var sketch = newSketch(context, id + "F44", { "sketchPlane" : qUnion([Q0])});
            skLineSegment(sketch, "E93", {"start": v(-115.62, 140.97) * mm, "end": v(-117.38, 140.97) * mm});
            skLineSegment(sketch, "E94", {"start": v(-115.62, 140.97) * mm, "end": v(-115.47, 144.2) * mm});
            skArc(sketch, "E95", {"start": v(-117.38, 140.97) * mm, "mid": v(-116.1, 142.39) * mm, "end": v(-115.47, 144.2) * mm});
            skSolve(sketch);
        }
        {
            var Q0;
            Q0=makeQuery(id+"F44.imprint","IMPRINT",FACE,{"disambiguationData":[TD([[makeQuery(id+"F44.imprint","IMPRINT",EDGE,{"derivedFrom":sQuery(id+"F44.wireOp",EDGE,"E93")}),1.0]])]});
            extrude(context, id + "F45", {"entities" : qUnion([Q0]), "operationType" : NewBodyOperationType.REMOVE, "oppositeDirection" : true, "depth" : 0.24 * mm});
        }
        {
            var Q0;
            Q0=qCreatedBy(id+"F25.planeOp",FACE);
            cPlane(context, id + "F46", {"entities" : qUnion([Q0]), "cplaneType" : CPlaneType.OFFSET, "offset" : 25.4 * mm, "width" : 152.4 * mm, "height" : 152.4 * mm});
        }
        {
            var Q0;
            Q0=qCreatedBy(id+"F46.planeOp",FACE);
            var sketch = newSketch(context, id + "F47", { "sketchPlane" : qUnion([Q0])});
            skLineSegment(sketch, "E96", {"start": v(0, 0) * mm, "end": v(0, 151.77) * mm, "construction": true});
            skLineSegment(sketch, "E97", {"start": v(-7.87, 177.8) * mm, "end": v(-7.87, 167.64) * mm});
            skLineSegment(sketch, "E98", {"start": v(7.87, 167.64) * mm, "end": v(7.87, 177.8) * mm});
            skArc(sketch, "E99", {"start": v(-7.87, 167.64) * mm, "mid": v(-10.16, 160.4) * mm, "end": v(-7.87, 153.16) * mm});
            skArc(sketch, "E100", {"start": v(7.87, 153.16) * mm, "mid": v(10.16, 160.4) * mm, "end": v(7.87, 167.64) * mm});
            skArc(sketch, "E101", {"start": v(-7.87, 153.16) * mm, "mid": v(0, 151.77) * mm, "end": v(7.87, 153.16) * mm});
            skPoint(sketch, "E102.orphan", {"position": v(0, 167.64) * mm});
            skLineSegment(sketch, "E103", {"start": v(-7.87, 177.8) * mm, "end": v(7.87, 177.8) * mm});
            skPoint(sketch, "E104.start.orphan", {"position": v(0, 160.4) * mm});
            skArc(sketch, "E105.2", {"start": v(9, 151.69) * mm, "mid": v(11.27, 156.07) * mm, "end": v(11.93, 160.97) * mm});
            skArc(sketch, "E105.4", {"start": v(-9, 151.69) * mm, "mid": v(0, 149.99) * mm, "end": v(9, 151.69) * mm});
            skArc(sketch, "E105.5", {"start": v(-11.93, 160.97) * mm, "mid": v(-11.27, 156.07) * mm, "end": v(-9, 151.69) * mm});
            skLineSegment(sketch, "E106", {"start": v(11.93, 159.83) * mm, "end": v(11.93, 177.8) * mm});
            skLineSegment(sketch, "E107", {"start": v(-11.93, 159.83) * mm, "end": v(-11.93, 177.8) * mm});
            skLineSegment(sketch, "E108", {"start": v(-7.87, 177.8) * mm, "end": v(-11.93, 177.8) * mm});
            skLineSegment(sketch, "E109", {"start": v(7.87, 177.8) * mm, "end": v(11.93, 177.8) * mm});
            skSolve(sketch);
        }
        {
            var Q0;
            Q0=makeQuery(id+"F47.imprint","IMPRINT",FACE,{"disambiguationData":[TD([[makeQuery(id+"F47.imprint","IMPRINT",EDGE,{"derivedFrom":sQuery(id+"F47.wireOp",EDGE,"E97")}),1.0]])]});
            var Q1;
            Q1=makeQuery(id+"F47.imprint","IMPRINT",FACE,{"disambiguationData":[TD([[makeQuery(id+"F47.imprint","IMPRINT",EDGE,{"derivedFrom":sQuery(id+"F47.wireOp",EDGE,"E97")}),-1.0]])]});
            extrude(context, id + "F48", {"entities" : qUnion([Q0, Q1]), "operationType" : NewBodyOperationType.REMOVE, "oppositeDirection" : true, "depth" : 50.8 * mm});
        }
        {
            var Q0;
            Q0=qCreatedBy(id+"F25.planeOp",FACE);
            var sketch = newSketch(context, id + "F49", { "sketchPlane" : qUnion([Q0])});
            skLineSegment(sketch, "E110", {"start": v(0, 0) * mm, "end": v(0, 151.77) * mm, "construction": true});
            skLineSegment(sketch, "E111", {"start": v(-7.87, 177.8) * mm, "end": v(-7.87, 167.64) * mm});
            skLineSegment(sketch, "E112", {"start": v(7.87, 167.64) * mm, "end": v(7.87, 177.8) * mm});
            skArc(sketch, "E113", {"start": v(-7.87, 167.64) * mm, "mid": v(-10.16, 160.4) * mm, "end": v(-7.87, 153.16) * mm});
            skArc(sketch, "E114", {"start": v(7.87, 153.16) * mm, "mid": v(10.16, 160.4) * mm, "end": v(7.87, 167.64) * mm});
            skArc(sketch, "E115", {"start": v(-7.87, 153.16) * mm, "mid": v(0, 151.77) * mm, "end": v(7.87, 153.16) * mm});
            skPoint(sketch, "E116.orphan", {"position": v(0, 167.64) * mm});
            skLineSegment(sketch, "E117", {"start": v(-7.87, 177.8) * mm, "end": v(7.87, 177.8) * mm});
            skPoint(sketch, "E118.start.orphan", {"position": v(0, 160.4) * mm});
            skArc(sketch, "E119.2", {"start": v(9, 151.69) * mm, "mid": v(11.27, 156.07) * mm, "end": v(11.93, 160.97) * mm});
            skArc(sketch, "E119.4", {"start": v(-9, 151.69) * mm, "mid": v(0, 149.99) * mm, "end": v(9, 151.69) * mm});
            skArc(sketch, "E119.5", {"start": v(-11.93, 160.97) * mm, "mid": v(-11.27, 156.07) * mm, "end": v(-9, 151.69) * mm});
            skLineSegment(sketch, "E120", {"start": v(11.93, 159.83) * mm, "end": v(11.93, 177.8) * mm});
            skLineSegment(sketch, "E121", {"start": v(-11.93, 159.83) * mm, "end": v(-11.93, 177.8) * mm});
            skLineSegment(sketch, "E122", {"start": v(-7.87, 177.8) * mm, "end": v(-11.93, 177.8) * mm});
            skLineSegment(sketch, "E123", {"start": v(7.87, 177.8) * mm, "end": v(11.93, 177.8) * mm});
            skSolve(sketch);
        }
        {
            var Q0;
            Q0=makeQuery(id+"F49.imprint","IMPRINT",FACE,{"disambiguationData":[TD([[makeQuery(id+"F49.imprint","IMPRINT",EDGE,{"derivedFrom":sQuery(id+"F49.wireOp",EDGE,"E111")}),-1.0]])]});
            var Q1;
            Q1=makeQuery(id+"F8.opPattern","COPY",FACE,{"derivedFrom":makeQuery(id+"F1.opRevolve","SWEPT_FACE",FACE,{"disambiguationData":[OSD([sQuery(id+"F0.wireOp",EDGE,"E15")])]}),"instanceName":"1"});
            var Q2;
            Q2=makeQuery(id+"F1.opRevolve","SWEPT_FACE",FACE,{"disambiguationData":[OSD([sQuery(id+"F0.wireOp",EDGE,"E22")])]});
            extrude(context, id + "F50", {"entities" : qUnion([Q0]), "endBound" : BoundingType.UP_TO_SURFACE, "endBoundEntityFace" : qUnion([Q1]), "depth" : 25.4 * mm, "hasSecondDirection" : true, "secondDirectionBound" : SecondDirectionBoundingType.UP_TO_SURFACE, "secondDirectionOppositeDirection" : true, "secondDirectionBoundEntityFace" : qUnion([Q2]), "secondDirectionDepth" : 25.4 * mm});
        }
        {
            var Q0;
            Q0=makeQuery(id+"F50.opExtrude","SWEPT_FACE",FACE,{"disambiguationData":[OSD([sQuery(id+"F49.wireOp",EDGE,"E120")])]});
            var sketch = newSketch(context, id + "F51", { "sketchPlane" : qUnion([Q0])});
            skLineSegment(sketch, "E124", {"start": v(-97.98, 172.74) * mm, "end": v(-110.32, 177.33) * mm});
            skLineSegment(sketch, "E125", {"start": v(-110.32, 177.33) * mm, "end": v(-90.5, 169.96) * mm});
            skLineSegment(sketch, "E126", {"start": v(-90.5, 169.96) * mm, "end": v(-118.42, 180.34) * mm});
            skLineSegment(sketch, "E127", {"start": v(-118.42, 180.34) * mm, "end": v(-116.7, 184.99) * mm});
            skLineSegment(sketch, "E128", {"start": v(-116.7, 184.99) * mm, "end": v(-94.35, 182.99) * mm});
            skLineSegment(sketch, "E129", {"start": v(-94.35, 182.99) * mm, "end": v(-90.5, 169.96) * mm});
            skSolve(sketch);
        }
        {
            var Q0;
            {var subQ0=sQuery(id+"F51.wireOp",EDGE,"E127");Q0=makeQuery(id+"F51.imprint","IMPRINT",FACE,{"disambiguationData":[TD([[makeQuery(id+"F51.imprint","IMPRINT",EDGE,{"derivedFrom":subQ0}),-1.0]])]});}
            var Q1;
            {var subQ0=sQuery(id+"F51.wireOp",EDGE,"E126");var subQ10=makeQuery(id+"F51.imprint","IMPRINT",VERTEX,{"disambiguationData":[OD(0.0)],"derivedFrom":subQ0});Q1=makeQuery(id+"F51.imprint","IMPRINT",FACE,{"disambiguationData":[TD([[makeQuery(id+"F51.imprint","IMPRINT",EDGE,{"disambiguationData":[TD([[subQ10,-1.0]])],"derivedFrom":subQ0}),-1.0]])]});}
            extrude(context, id + "F52", {"entities" : qUnion([Q0, Q1]), "operationType" : NewBodyOperationType.REMOVE, "oppositeDirection" : true, "depth" : 5.08 * mm});
        }
        {
            var Q0;
            Q0=makeQuery(id+"F50.opExtrude","SWEPT_FACE",FACE,{"disambiguationData":[OSD([sQuery(id+"F49.wireOp",EDGE,"E120")])]});
            var sketch = newSketch(context, id + "F53", { "sketchPlane" : qUnion([Q0])});
            skArc(sketch, "E130", {"start": v(-110.32, 177.33) * mm, "mid": v(-113.6, 176.96) * mm, "end": v(-115.24, 174.1) * mm});
            skLineSegment(sketch, "E131", {"start": v(-110.32, 177.33) * mm, "end": v(-109.67, 179.08) * mm});
            skLineSegment(sketch, "E132", {"start": v(-109.67, 179.08) * mm, "end": v(-117.54, 181.05) * mm});
            skLineSegment(sketch, "E133", {"start": v(-115.24, 174.1) * mm, "end": v(-117.43, 174.1) * mm});
            skLineSegment(sketch, "E134", {"start": v(-117.43, 174.1) * mm, "end": v(-117.54, 181.05) * mm});
            skSolve(sketch);
        }
        {
            var Q0;
            {var subQ1=sQuery(id+"F53.wireOp",EDGE,"E131");Q0=makeQuery(id+"F53.imprint","IMPRINT",FACE,{"disambiguationData":[TD([[makeQuery(id+"F53.imprint","IMPRINT",EDGE,{"derivedFrom":subQ1}),1.0]])]});}
            var Q1;
            {var subQ0=sQuery(id+"F53.wireOp",EDGE,"E130");var subQ1=makeQuery(id+"F52.boolean.opBoolean","COPY",EDGE,{"derivedFrom":makeQuery(id+"F52.opExtrude","CAP_EDGE",EDGE,{"disambiguationData":[OSD([sQuery(id+"F51.wireOp",EDGE,"E126")])],"isStart":true})});var subQ2=makeQuery(id+"F53.imprint","INTERSECT",VERTEX,{"derivedFrom":[subQ1,subQ0]});Q1=makeQuery(id+"F53.imprint","IMPRINT",FACE,{"disambiguationData":[TD([[makeQuery(id+"F53.imprint","IMPRINT",EDGE,{"disambiguationData":[TD([[subQ2,-1.0]])],"derivedFrom":subQ0}),-1.0]])]});}
            extrude(context, id + "F54", {"entities" : qUnion([Q0, Q1]), "operationType" : NewBodyOperationType.REMOVE, "oppositeDirection" : true, "depth" : 5.08 * mm});
        }
        {
            var Q0;
            Q0=makeQuery(id+"F50.opExtrude","SWEPT_FACE",FACE,{"disambiguationData":[OSD([sQuery(id+"F49.wireOp",EDGE,"E120")])]});
            var sketch = newSketch(context, id + "F55", { "sketchPlane" : qUnion([Q0])});
            skArc(sketch, "E135", {"start": v(-94.26, 167.77) * mm, "mid": v(-95.38, 170.8) * mm, "end": v(-97.98, 172.74) * mm});
            skLineSegment(sketch, "E136", {"start": v(-97.98, 172.74) * mm, "end": v(-96.3, 175.92) * mm});
            skLineSegment(sketch, "E137", {"start": v(-96.3, 175.92) * mm, "end": v(-88.68, 171.9) * mm});
            skLineSegment(sketch, "E138", {"start": v(-88.68, 171.9) * mm, "end": v(-92.08, 166.46) * mm});
            skLineSegment(sketch, "E139", {"start": v(-94.26, 167.77) * mm, "end": v(-92.5, 166.84) * mm});
            skLineSegment(sketch, "E140", {"start": v(-92.5, 166.84) * mm, "end": v(-92.08, 166.46) * mm});
            skSolve(sketch);
        }
        {
            var Q0;
            {var subQ0=sQuery(id+"F55.wireOp",EDGE,"E135");var subQ1=makeQuery(id+"F52.boolean.opBoolean","COPY",EDGE,{"derivedFrom":makeQuery(id+"F52.opExtrude","CAP_EDGE",EDGE,{"disambiguationData":[OSD([sQuery(id+"F51.wireOp",EDGE,"E126")])],"isStart":true})});var subQ2=makeQuery(id+"F55.imprint","INTERSECT",VERTEX,{"derivedFrom":[subQ1,subQ0]});Q0=makeQuery(id+"F55.imprint","IMPRINT",FACE,{"disambiguationData":[TD([[makeQuery(id+"F55.imprint","IMPRINT",EDGE,{"disambiguationData":[TD([[subQ2,1.0]])],"derivedFrom":subQ1}),1.0]])]});}
            var Q1;
            {var subQ0=sQuery(id+"F55.wireOp",EDGE,"E136");Q1=makeQuery(id+"F55.imprint","IMPRINT",FACE,{"disambiguationData":[TD([[makeQuery(id+"F55.imprint","IMPRINT",EDGE,{"derivedFrom":subQ0}),-1.0]])]});}
            extrude(context, id + "F56", {"entities" : qUnion([Q0, Q1]), "operationType" : NewBodyOperationType.REMOVE, "oppositeDirection" : true, "depth" : 5.08 * mm});
        }
        {
            var Q0;
            Q0=makeQuery(id+"F50.opExtrude","SWEPT_FACE",FACE,{"disambiguationData":[OSD([sQuery(id+"F49.wireOp",EDGE,"E121")])]});
            var sketch = newSketch(context, id + "F57", { "sketchPlane" : qUnion([Q0])});
            skLineSegment(sketch, "E141", {"start": v(110.32, 177.33) * mm, "end": v(97.98, 172.74) * mm});
            skLineSegment(sketch, "E142", {"start": v(97.98, 172.74) * mm, "end": v(120.99, 181.3) * mm});
            skLineSegment(sketch, "E143", {"start": v(120.99, 181.3) * mm, "end": v(87.56, 168.87) * mm});
            skLineSegment(sketch, "E144", {"start": v(87.56, 168.87) * mm, "end": v(87.36, 169.4) * mm});
            skLineSegment(sketch, "E145", {"start": v(87.36, 169.4) * mm, "end": v(87.56, 182.32) * mm});
            skLineSegment(sketch, "E146", {"start": v(87.56, 182.32) * mm, "end": v(120.99, 181.3) * mm});
            skSolve(sketch);
        }
        {
            var Q0;
            {var subQ0=sQuery(id+"F57.wireOp",EDGE,"E144");Q0=makeQuery(id+"F57.imprint","IMPRINT",FACE,{"disambiguationData":[TD([[makeQuery(id+"F57.imprint","IMPRINT",EDGE,{"derivedFrom":subQ0}),-1.0]])]});}
            var Q1;
            {var subQ0=sQuery(id+"F57.wireOp",EDGE,"E143");var subQ10=makeQuery(id+"F57.imprint","IMPRINT",VERTEX,{"disambiguationData":[OD(0.0)],"derivedFrom":subQ0});Q1=makeQuery(id+"F57.imprint","IMPRINT",FACE,{"disambiguationData":[TD([[makeQuery(id+"F57.imprint","IMPRINT",EDGE,{"disambiguationData":[TD([[subQ10,-1.0]])],"derivedFrom":subQ0}),-1.0]])]});}
            extrude(context, id + "F58", {"entities" : qUnion([Q0, Q1]), "operationType" : NewBodyOperationType.REMOVE, "oppositeDirection" : true, "depth" : 5.08 * mm});
        }
        {
            var Q0;
            Q0=makeQuery(id+"F50.opExtrude","SWEPT_FACE",FACE,{"disambiguationData":[OSD([sQuery(id+"F49.wireOp",EDGE,"E121")])]});
            var sketch = newSketch(context, id + "F59", { "sketchPlane" : qUnion([Q0])});
            skArc(sketch, "E147", {"start": v(115.24, 174.1) * mm, "mid": v(113.6, 176.96) * mm, "end": v(110.32, 177.33) * mm});
            skLineSegment(sketch, "E148", {"start": v(115.24, 174.1) * mm, "end": v(120.55, 174.1) * mm});
            skLineSegment(sketch, "E149", {"start": v(120.55, 174.1) * mm, "end": v(120.07, 180.05) * mm});
            skLineSegment(sketch, "E150", {"start": v(120.07, 180.05) * mm, "end": v(110.52, 180.05) * mm});
            skLineSegment(sketch, "E151", {"start": v(110.52, 180.05) * mm, "end": v(110.32, 177.33) * mm});
            skSolve(sketch);
        }
        {
            var Q0;
            {var subQ0=sQuery(id+"F59.wireOp",EDGE,"E147");var subQ1=makeQuery(id+"F58.boolean.opBoolean","COPY",EDGE,{"derivedFrom":makeQuery(id+"F58.opExtrude","CAP_EDGE",EDGE,{"disambiguationData":[OSD([sQuery(id+"F57.wireOp",EDGE,"E143")])],"isStart":true})});var subQ2=makeQuery(id+"F59.imprint","INTERSECT",VERTEX,{"derivedFrom":[subQ1,subQ0]});Q0=makeQuery(id+"F59.imprint","IMPRINT",FACE,{"disambiguationData":[TD([[makeQuery(id+"F59.imprint","IMPRINT",EDGE,{"disambiguationData":[TD([[subQ2,1.0]])],"derivedFrom":subQ0}),-1.0]])]});}
            var Q1;
            {var subQ0=sQuery(id+"F59.wireOp",EDGE,"E148");Q1=makeQuery(id+"F59.imprint","IMPRINT",FACE,{"disambiguationData":[TD([[makeQuery(id+"F59.imprint","IMPRINT",EDGE,{"derivedFrom":subQ0}),1.0]])]});}
            extrude(context, id + "F60", {"entities" : qUnion([Q0, Q1]), "operationType" : NewBodyOperationType.REMOVE, "oppositeDirection" : true, "depth" : 5.08 * mm});
        }
        {
            var Q0;
            Q0=makeQuery(id+"F50.opExtrude","SWEPT_FACE",FACE,{"disambiguationData":[OSD([sQuery(id+"F49.wireOp",EDGE,"E121")])]});
            var sketch = newSketch(context, id + "F61", { "sketchPlane" : qUnion([Q0])});
            skArc(sketch, "E152", {"start": v(97.98, 172.74) * mm, "mid": v(95.38, 170.8) * mm, "end": v(94.26, 167.77) * mm});
            skLineSegment(sketch, "E153", {"start": v(94.26, 167.77) * mm, "end": v(90.1, 167.77) * mm});
            skLineSegment(sketch, "E154", {"start": v(90.1, 167.77) * mm, "end": v(89.2, 176.46) * mm});
            skLineSegment(sketch, "E155", {"start": v(89.2, 176.46) * mm, "end": v(98.03, 178.16) * mm});
            skLineSegment(sketch, "E156", {"start": v(98.03, 178.16) * mm, "end": v(97.98, 172.74) * mm});
            skSolve(sketch);
        }
        {
            var Q0;
            {var subQ0=sQuery(id+"F61.wireOp",EDGE,"E152");var subQ1=makeQuery(id+"F58.boolean.opBoolean","COPY",EDGE,{"derivedFrom":makeQuery(id+"F58.opExtrude","CAP_EDGE",EDGE,{"disambiguationData":[OSD([sQuery(id+"F57.wireOp",EDGE,"E143")])],"isStart":true})});var subQ2=makeQuery(id+"F61.imprint","INTERSECT",VERTEX,{"derivedFrom":[subQ1,subQ0]});Q0=makeQuery(id+"F61.imprint","IMPRINT",FACE,{"disambiguationData":[TD([[makeQuery(id+"F61.imprint","IMPRINT",EDGE,{"disambiguationData":[TD([[subQ2,-1.0]])],"derivedFrom":subQ1}),1.0]])]});}
            var Q1;
            {var subQ0=sQuery(id+"F61.wireOp",EDGE,"E153");Q1=makeQuery(id+"F61.imprint","IMPRINT",FACE,{"disambiguationData":[TD([[makeQuery(id+"F61.imprint","IMPRINT",EDGE,{"derivedFrom":subQ0}),-1.0]])]});}
            extrude(context, id + "F62", {"entities" : qUnion([Q0, Q1]), "operationType" : NewBodyOperationType.REMOVE, "oppositeDirection" : true, "depth" : 5.08 * mm});
        }
    });
